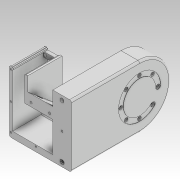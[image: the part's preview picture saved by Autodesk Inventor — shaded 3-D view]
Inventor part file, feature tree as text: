
AUTODESK INVENTOR PART (.ipt)
format: ipt  version: 2020 (Build 240168000, 168)  size: 1,394,176 bytes
history: native  units: mm
features: sketch x50, extrude x47, plane x9, projected_geometry x7, fillet x6, chamfer x3, revolve x3, pattern_circular x2, loft x1, mirror x1, other x1
ambient origin geometry x8: Origin, YZ Plane, XZ Plane, XY Plane, X Axis, Y Axis, Z Axis, Center Point
bodies: Solid1 (feature_tree)
feature tree (130):
  extrude  "Extrusion1"  Depth=50.0mm
  extrude  "Extrusion2"  Depth=100.0mm TaperAngle=0.0deg
  extrude  "Extrusion3"  TaperAngle=0.0deg  [1 undecoded]
  extrude  "Extrusion4"  Depth=10.0mm
  extrude  "Extrusion5"  Depth=1.0mm
  pattern_circular  "Circular Pattern1"  Count=8 Angle=360.0deg
  plane  "Work Plane1"
  plane  "Work Plane2"
  extrude  "Extrusion6"  Depth=30.0mm
  extrude  "Extrusion7"  Depth=10.0mm
  extrude  "Extrusion8"  Depth=10.0mm
  extrude  "Extrusion9"  [1 undecoded]
  chamfer  "Chamfer1"  Distance=10.0mm
  extrude  "Extrusion13"  Depth=10.0mm TaperAngle=0.0deg
  extrude  "Extrusion14"  Depth=3.0mm TaperAngle=0.0deg
  extrude  "Extrusion15"  Depth=2.0mm
  extrude  "Extrusion16"  Depth=3.0mm
  extrude  "Extrusion17"  Depth=80.5mm
  extrude  "Extrusion18"  Depth=60.0mm
  extrude  "Extrusion19"  Depth=80.0mm TaperAngle=360.0deg
  extrude  "Extrusion20"  Depth=15.5mm TaperAngle=0.0deg
  fillet  "Fillet2"  Radius=22.1mm
  pattern_circular  "Circular Pattern2"  Count=8 Angle=360.0deg
  extrude  "Extrusion21"  Depth=10.0mm
  extrude  "Extrusion22"  Depth=7.0mm
  plane  "Work Plane3"
  revolve  "Revolution1"  [1 undecoded]
  revolve  "Revolution2"  [1 undecoded]
  plane  "Work Plane4"
  extrude  "Extrusion23"  Depth=96.8mm TaperAngle=0.0deg
  extrude  "Extrusion24"  Depth=2.5mm
  fillet  "Fillet3"  Radius=5.2mm
  loft  "Loft1"
  extrude  "Extrusion25"  TaperAngle=90.0deg  [1 undecoded]
  extrude  "Extrusion26"  Depth=25.0mm
  extrude  "Extrusion27"  Depth=19.0mm
  extrude  "Extrusion28"  Depth=2.7mm
  plane  "Work Plane5"
  extrude  "Extrusion29"  Depth=5.5mm
  extrude  "Extrusion30"  TaperAngle=90.0deg  [1 undecoded]
  extrude  "Extrusion32"  Depth=2.0mm TaperAngle=0.0deg
  extrude  "Extrusion35"  Depth=6.0mm
  revolve  "Revolution3"  [1 undecoded]
  extrude  "Extrusion36"  [1 undecoded]
  plane  "Work Plane7"
  extrude  "Extrusion37"  Depth=1.0mm TaperAngle=0.0deg
  extrude  "Extrusion38"  Depth=5.0mm
  mirror  "Mirror1"
  extrude  "Extrusion39"  TaperAngle=0.0deg  [1 undecoded]
  extrude  "Extrusion40"  Depth=3.0mm
  extrude  "Extrusion41"  Depth=10.0mm
  chamfer  "Chamfer3"  [1 undecoded]
  fillet  "Fillet5"  [1 undecoded]
  extrude  "Extrusion42"  Depth=10.0mm TaperAngle=0.0deg
  extrude  "Extrusion43"  Depth=5.0mm
  plane  "Work Plane8"
  extrude  "Extrusion44"  Depth=2.25mm
  plane  "Work Plane9"
  extrude  "Extrusion45"  Depth=52.0mm TaperAngle=0.0deg
  extrude  "Extrusion46"  Depth=10.0mm
  fillet  "Fillet8"  Radius=1.0mm
  fillet  "Fillet6"  Radius=3.0mm
  fillet  "Fillet7"  [1 undecoded]
  sketch  "Sketch55"  dims[d137=1.0mm d138=0.0mm d139=-7.0mm]
  plane  "Work Plane10"
  extrude  "Extrusion48"  Depth=1.0mm
  extrude  "Extrusion49"  TaperAngle=90.0deg  [1 undecoded]
  extrude  "Extrusion50"  Depth=60.0mm
  extrude  "Extrusion51"  Depth=3.0mm
  extrude  "Extrusion52"  Depth=10.0mm TaperAngle=360.0deg
  chamfer  "Chamfer4"  Distance=52.0mm
  sketch  "Sketch62"  dims[d160=6.0mm d177=255.0mm d178=0.0mm d179=5.0mm d180=2.25mm d181=52.0mm d182=0.0mm d183=16.1mm d184=1.0mm d185=3.0mm d186=30.0deg d187=1.0mm d188=90.0deg d189=60.0mm d190=3.0mm d191=80.0mm d193=360.0deg d195=52.0mm d196=0.0mm d197=8.0mm d198=0.5mm d199=0.0mm d200=6.0mm d201=1.2mm d202=0.0mm d203=15.0mm d204=20.0mm d205=10.0mm d206=0.0mm d207=1.0mm d208=22.0mm d209=2.0mm d210=0.0mm d211=0.0mm d212=2.0mm d213=2.0mm d214=0.0mm d215=2.0mm d216=2.0mm d217=45.0deg d218=3.0mm d219=5.0mm d220=2.0mm d221=0.0mm d223=30.0mm d224=3.5mm d225=32.0mm d226=0.0mm d227=-6.0mm d229=32.0mm d230=0.0mm d231=12.0mm d232=-17.0mm d233=2.0mm d234=3.0mm d235=30.0mm d237=30.0mm d238=10.0mm d240=10.0mm d242=10.0mm d243=11.0mm d244=0.0mm d245=7.0mm d246=102.5mm d247=0.0mm d248=3.0mm d249=1.0mm d250=3.0mm d254=55.0mm d255=0.0mm d256=0.0mm d257=11.0mm d258=1.5mm d259=1.5mm d260=1.8mm d261=0.0mm d262=5.0mm d263=8.0mm d264=2.0mm d265=3.0mm d266=3.0mm d267=5.55mm d268=0.0mm d269=2.5mm d270=50.0mm d271=0.0mm d272=10.0mm d273=8.0mm d274=3.5mm d276=4.0mm d277=4.0mm d278=5.0mm d279=4.0mm d280=0.0mm d281=4.0mm d282=2.0mm d283=45.0deg d284=7.0mm d285=0.15mm d286=10.0mm d287=0.0mm d288=10.0mm d289=0.0mm]
  extrude  "Extrusion53"  Depth=10.0mm
  extrude  "Extrusion54"  Depth=10.0mm TaperAngle=0.0deg
  sketch  "Sketch1"  dims[d0=50.0mm d1=250.0mm]
  sketch  "Sketch2"  dims[d2=50.0mm d3=100.0mm d4=0.0mm]
  sketch  "Sketch4"  dims[d5=5.0mm d7=0.0mm d8=0.0mm]
  sketch  "Sketch5"  dims[d11=10.0mm d12=0.0mm d14=85.0mm]
  sketch  "Sketch7"  dims[d15=1.0mm d16=0.0mm d17=30.0mm]
  projected_geometry  "Projected Loop1"
  sketch  "Sketch8"  dims[d18=3.3mm]
  projected_geometry  "Projected Loop2"
  projected_geometry  "Projected Loop4"
  sketch  "Sketch9"  dims[d19=15.0mm d20=0.0mm d21=80.0mm d22=360.0deg]
  sketch  "Sketch10"  dims[d24=30.0mm d25=30.0mm]
  sketch  "Sketch14"  dims[d30=-5.0mm d31=10.0mm]
  sketch  "Sketch15"  dims[d32=10.0mm d33=10.0mm]
  sketch  "Sketch16"  dims[d34=31.5mm d35=0.0mm d36=-5.0mm d38=10.0mm d39=0.0mm]
  sketch  "Sketch17"  dims[d40=22.1mm d41=10.0mm d42=0.0mm]
  sketch  "Sketch18"  dims[d43=5.0mm d44=3.0mm d45=0.0mm]
  sketch  "Sketch19"  dims[d56=3.0mm d57=2.0mm d58=45.0deg d62=95.1mm]
  sketch  "Sketch20"  dims[d63=10.0mm d64=0.0mm d65=3.0mm]
  sketch  "Sketch21"  dims[d66=0.5mm d67=0.0mm d68=80.5mm]
  sketch  "Sketch22"  dims[d69=16.5mm d70=0.0mm d71=60.0mm]
  sketch  "Sketch23"  dims[d72=3.2mm d73=80.0mm d75=360.0deg]
  other  "Work Axis1"
  sketch  "Sketch24"  dims[d77=15.5mm d78=0.0mm d79=15.5mm d80=0.0mm d81=22.1mm]
  projected_geometry  "Projected Loop5"
  projected_geometry  "Projected Loop6"
  sketch  "Sketch26"  dims[d82=0.0mm d83=0.0mm]
  sketch  "Sketch27"  dims[d84=76.0mm]
  sketch  "Sketch28"  dims[d85=0.1mm d86=0.0mm]
  sketch  "Sketch29"  dims[d87=15.0mm]
  sketch  "Sketch30"  dims[d88=2.0mm]
  sketch  "Sketch31"  dims[d89=22.5mm]
  sketch  "Sketch32"  dims[d90=0.8mm d91=0.0mm]
  sketch  "Sketch33"  dims[d92=0.2mm d93=80.0mm d94=360.0deg]
  projected_geometry  "Projected Loop7"
  sketch  "Sketch34"  dims[d96=24.43461mm d97=10.0mm]
  sketch  "Sketch35"  dims[d98=6.25mm d99=7.0mm]
  sketch  "Sketch38"  dims[d100=6.25mm d101=7.0mm]
  sketch  "Sketch41"  dims[d102=5.0mm d103=0.0mm d104=25.0mm]
  sketch  "Sketch42"  dims[d105=16.1mm d106=96.8mm d107=0.0mm]
  sketch  "Sketch43"  dims[d108=0.0mm d109=2.5mm d110=5.2mm]
  sketch  "Sketch44"  dims[d111=1.0mm d112=5.0mm]
  sketch  "Sketch45"  dims[d113=5.2mm d114=90.0deg]
  sketch  "Sketch46"  dims[d115=15.0mm d116=25.0mm]
  sketch  "Sketch47"  dims[d117=25.0mm d118=19.0mm]
  projected_geometry  "Projected Loop8"
  sketch  "Sketch48"  dims[d119=19.0mm d120=2.7mm]
  sketch  "Sketch49"  dims[d122=4.0mm d123=0.0mm d124=5.5mm]
  sketch  "Sketch50"  dims[d125=2.0mm d126=0.0mm d127=90.0deg]
  sketch  "Sketch51"  dims[d128=2.0mm d129=18.8mm d130=0.0mm]
  sketch  "Sketch52"  dims[d131=111.25mm d132=0.0mm d133=6.0mm]
  sketch  "Sketch53"  dims[d134=4.0mm d135=0.0mm d136=1.0mm]
  sketch  "Sketch57"  dims[d140=1.0mm d141=1.0mm d142=0.0mm]
  sketch  "Sketch58"  dims[d143=7.0mm d144=5.0mm]
  sketch  "Sketch59"  dims[d145=6.0mm d146=0.0mm d147=90.0deg]
  sketch  "Sketch60"  dims[d148=0.0mm d149=90.0deg d150=3.0mm]
  sketch  "Sketch61"  dims[d151=10.0mm d152=0.0mm d155=110.0mm d156=0.0mm d157=0.0mm d159=30.0deg]
note: 13 required parameter values undecoded (feature->parameter linkage not recoverable at this tier; creation-order binding heuristic only, values carry confidence <= 0.55)